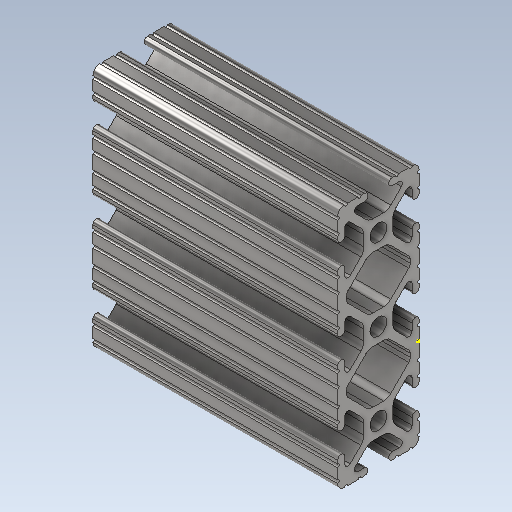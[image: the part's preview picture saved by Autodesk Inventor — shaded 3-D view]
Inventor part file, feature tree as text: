
AUTODESK INVENTOR PART (.ipt)
format: ipt  version: 2020 (Build 240168000, 168)  size: 482,304 bytes
history: native  units: in
note: dims shown in document units (in); Inventor stores cm internally (conversion verified against a paired STEP export)
features: sketch x2, extrude x1
ambient origin geometry x8: Origin, YZ Plane, XZ Plane, XY Plane, X Axis, Y Axis, Z Axis, Center Point
bodies: Solid1 (feature_tree)
feature tree (3):
  extrude  "Extrusion1"  [1 undecoded]
  sketch  "Sketch2"
  sketch  "Sketch1"  dims[d0=3.0in d1=0.0in]
note: 1 required parameter value undecoded (feature->parameter linkage not recoverable at this tier; creation-order binding heuristic only, values carry confidence <= 0.55)
